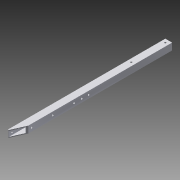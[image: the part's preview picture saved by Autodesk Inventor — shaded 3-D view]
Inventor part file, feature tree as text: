
AUTODESK INVENTOR PART (.ipt)
format: ipt  version: 2015 (Build 190159000, 159)  size: 149,504 bytes
history: native  units: in
note: dims shown in document units (in); Inventor stores cm internally (conversion verified against a paired STEP export)
features: sketch x5, hole x3, extrude x2, projected_geometry x1
ambient origin geometry x8: Origin, YZ Plane, XZ Plane, XY Plane, X Axis, Y Axis, Z Axis, Center Point
bodies: Solid1 (feature_tree)
feature tree (11):
  extrude  "Extrusion1"  Depth=1.0in
  hole  "Hole1"  [1 undecoded]
  hole  "Hole2"  [1 undecoded]
  extrude  "Extrusion4"  Depth=23.125in
  hole  "Hole3"  [1 undecoded]
  sketch  "Sketch1"  dims[d0=1.0in d1=1.0in]
  sketch  "Sketch2"  dims[d2=0.75in d3=0.75in]
  sketch  "Sketch3"  dims[d4=0.125in d5=0.125in]
  sketch  "Sketch6"  dims[d6=23.125in d7=0.0in d8=0.5in]
  projected_geometry  "Projected Loop3"
  sketch  "Sketch7"  dims[d9=0.5in d10=0.5in d11=5.5in d12=0.25in d13=0.75in d14=0.375in d15=0.25in d16=0.5635in d17=1.0in d18=0.8108in d19=0.5in d20=0.5in d21=0.5in d22=1.0in d23=8.375in d24=1.0in d25=0.5in d26=0.5in d27=0.25in d28=0.75in d29=0.375in d30=0.25in d31=0.5635in d32=1.0in d33=0.8108in d41=0.875in d42=2.0in d43=1.0in d44=0.0in d45=0.5in d46=2.5in d47=0.5in d48=0.5in d49=5.625in d50=8.75in d51=0.25in d52=0.75in d53=0.375in d54=0.25in d55=0.5635in d56=1.0in d57=0.8108in]
note: 3 required parameter values undecoded (feature->parameter linkage not recoverable at this tier; creation-order binding heuristic only, values carry confidence <= 0.55)
